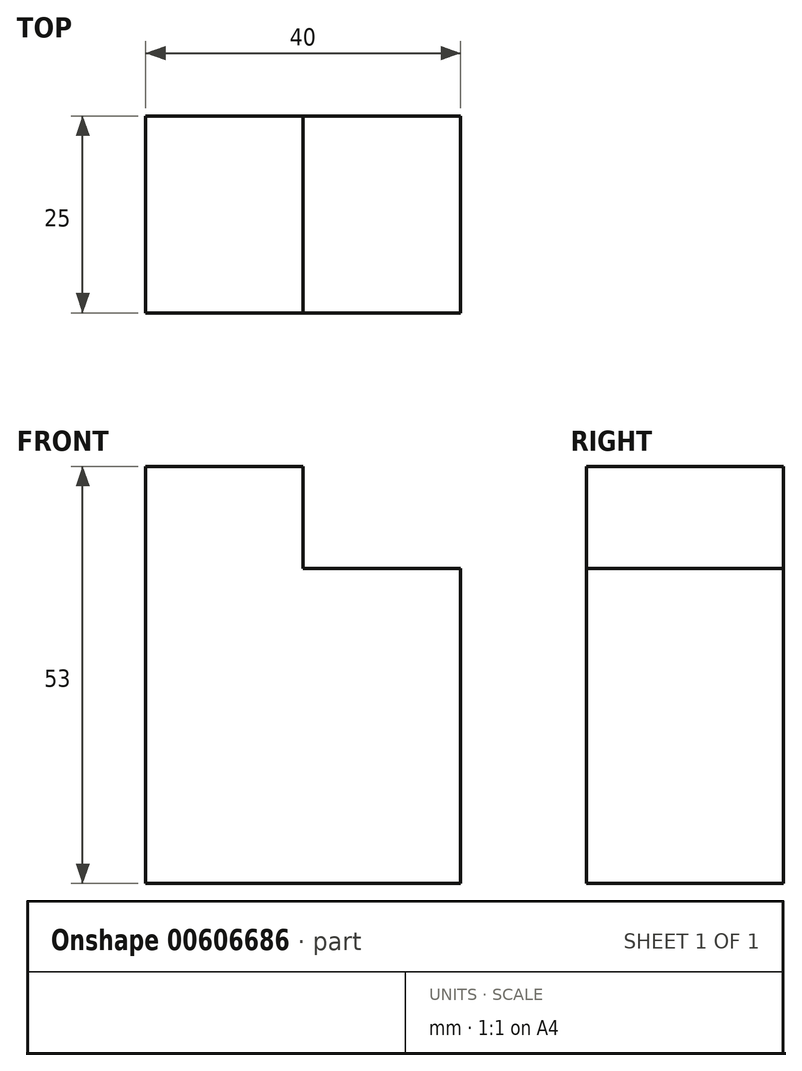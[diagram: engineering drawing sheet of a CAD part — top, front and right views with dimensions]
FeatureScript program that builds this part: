
annotation { "Feature Type Name" : "Feature", "Feature Type Description" : "" }
export const myFeature = defineFeature(function(context is Context, id is Id, definition is map)
    precondition{}
    {
        {
            var Q0;
            Q0=qCreatedBy(makeId("Front.planeOp"),FACE);
            var sketch = newSketch(context, id + "F0", { "sketchPlane" : qUnion([Q0])});
            skLineSegment(sketch, "E0", {"start": v(0, 0) * mm, "end": v(40, 0) * mm});
            skLineSegment(sketch, "E1", {"start": v(40, 0) * mm, "end": v(40, 40) * mm});
            skLineSegment(sketch, "E2", {"start": v(40, 40) * mm, "end": v(20, 40) * mm});
            skLineSegment(sketch, "E3", {"start": v(20, 40) * mm, "end": v(20, 53) * mm});
            skLineSegment(sketch, "E4", {"start": v(20, 53) * mm, "end": v(0, 53) * mm});
            skLineSegment(sketch, "E5", {"start": v(0, 53) * mm, "end": v(0, 0) * mm});
            skSolve(sketch);
        }
        {
            var Q0;
            Q0 = qSketchRegion(id + "F0", true);
            extrude(context, id + "F1", {"entities" : qUnion([Q0]), "depth" : 25 * mm, "offsetDistance" : 25 * mm});
        }
    });
